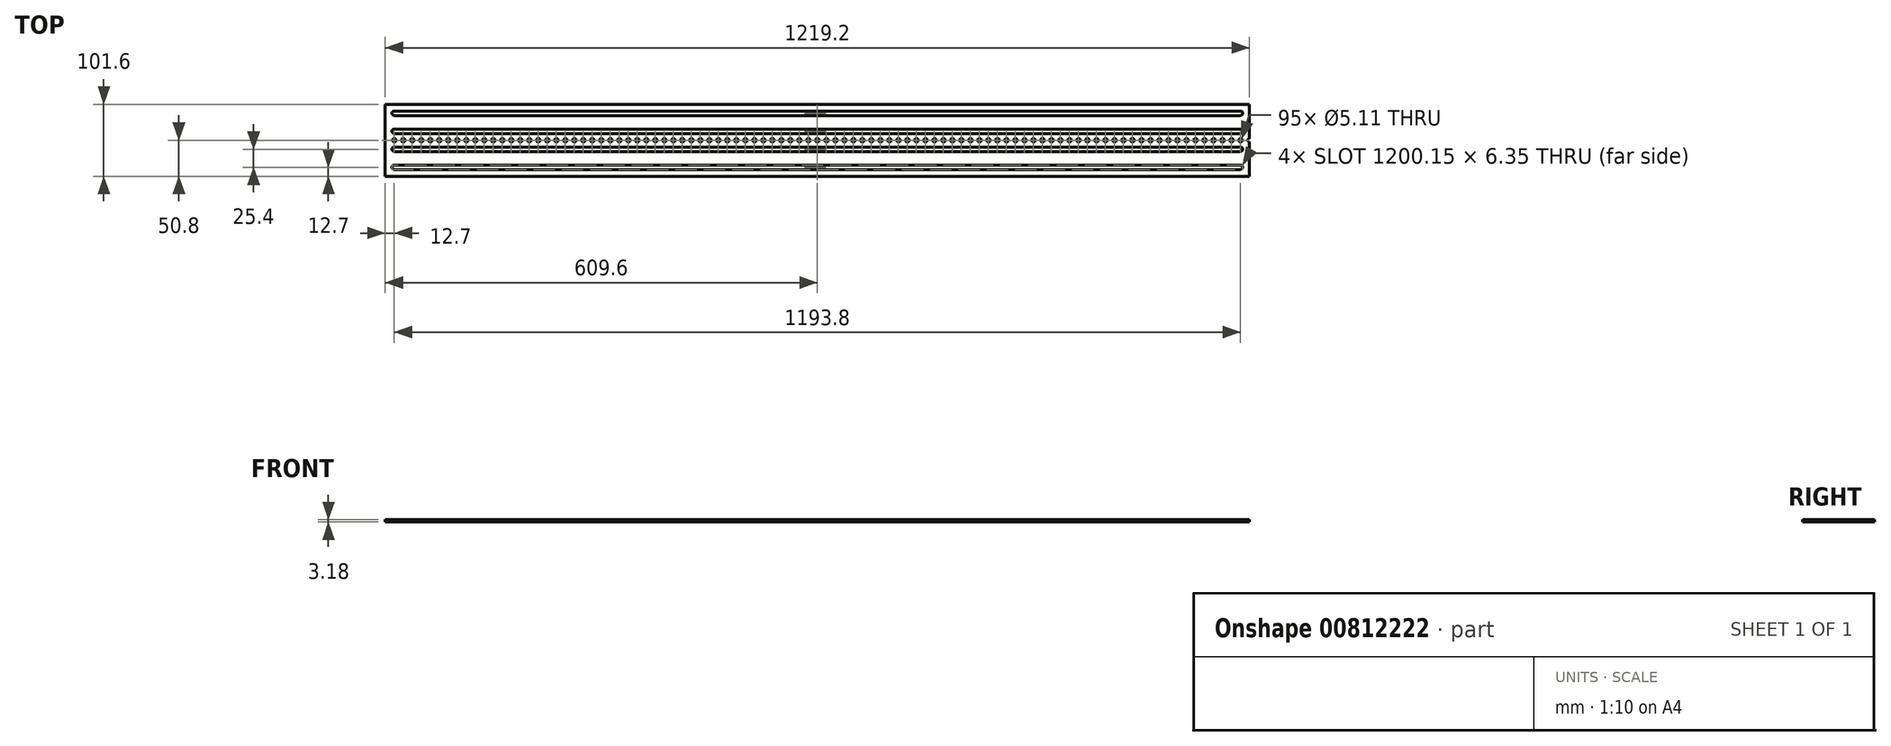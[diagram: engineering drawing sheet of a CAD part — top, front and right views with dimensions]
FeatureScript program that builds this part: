
annotation { "Feature Type Name" : "Feature", "Feature Type Description" : "" }
export const myFeature = defineFeature(function(context is Context, id is Id, definition is map)
    precondition{}
    {
        {
            var Q0;
            Q0=qCreatedBy(makeId("Top.planeOp"),FACE);
            var sketch = newSketch(context, id + "F0", { "sketchPlane" : qUnion([Q0])});
            skLineSegment(sketch, "E0.bottom", {"start": v(-609.6, -50.8) * mm, "end": v(609.6, -50.8) * mm});
            skLineSegment(sketch, "E0.top", {"start": v(-609.6, 50.8) * mm, "end": v(609.6, 50.8) * mm});
            skLineSegment(sketch, "E0.left", {"start": v(-609.6, -50.8) * mm, "end": v(-609.6, 50.8) * mm});
            skLineSegment(sketch, "E0.right", {"start": v(609.6, -50.8) * mm, "end": v(609.6, 50.8) * mm});
            skPoint(sketch, "E0.middle", {"position": v(0, 0) * mm});
            skLineSegment(sketch, "E1", {"start": v(-609.6, 25.4) * mm, "end": v(609.6, 25.4) * mm, "construction": true});
            skLineSegment(sketch, "E2", {"start": v(609.6, -25.4) * mm, "end": v(-609.6, -25.4) * mm, "construction": true});
            skLineSegment(sketch, "E3", {"start": v(0, -25.4) * mm, "end": v(0, 25.4) * mm, "construction": true});
            skLineSegment(sketch, "E4.bottom", {"start": v(-596.9, 12.7) * mm, "end": v(596.9, 12.7) * mm, "construction": true});
            skLineSegment(sketch, "E4.top", {"start": v(-596.9, -12.7) * mm, "end": v(596.9, -12.7) * mm, "construction": true});
            skLineSegment(sketch, "E4.left", {"start": v(-596.9, 12.7) * mm, "end": v(-596.9, -12.7) * mm, "construction": true});
            skLineSegment(sketch, "E4.right", {"start": v(596.9, 12.7) * mm, "end": v(596.9, -12.7) * mm, "construction": true});
            skArc(sketch, "E5", {"start": v(-596.9, 15.88) * mm, "mid": v(-600.08, 12.7) * mm, "end": v(-596.9, 9.53) * mm});
            skArc(sketch, "E6", {"start": v(-596.9, -9.53) * mm, "mid": v(-600.08, -12.7) * mm, "end": v(-596.9, -15.88) * mm});
            skArc(sketch, "E7", {"start": v(596.9, 9.53) * mm, "mid": v(600.08, 12.7) * mm, "end": v(596.9, 15.88) * mm});
            skArc(sketch, "E8", {"start": v(596.9, -15.88) * mm, "mid": v(600.08, -12.7) * mm, "end": v(596.9, -9.53) * mm});
            skLineSegment(sketch, "E9", {"start": v(596.9, 15.88) * mm, "end": v(-596.9, 15.87) * mm});
            skLineSegment(sketch, "E10", {"start": v(-596.9, 9.52) * mm, "end": v(596.9, 9.53) * mm});
            skLineSegment(sketch, "E11", {"start": v(-596.9, -9.53) * mm, "end": v(596.9, -9.53) * mm});
            skLineSegment(sketch, "E12", {"start": v(596.9, -15.88) * mm, "end": v(-596.9, -15.88) * mm});
            skCircle(sketch, "E13", {"center": v(-596.9, 0) * mm, "radius": 2.55 * mm});
            skCircle(sketch, "E14.1.0.0", {"center": v(-584.2, 0) * mm, "radius": 2.55 * mm});
            skCircle(sketch, "E14.2.0.0", {"center": v(-571.5, 0) * mm, "radius": 2.55 * mm});
            skCircle(sketch, "E14.3.0.0", {"center": v(-558.8, 0) * mm, "radius": 2.55 * mm});
            skCircle(sketch, "E14.4.0.0", {"center": v(-546.1, 0) * mm, "radius": 2.55 * mm});
            skCircle(sketch, "E14.5.0.0", {"center": v(-533.4, 0) * mm, "radius": 2.55 * mm});
            skCircle(sketch, "E14.6.0.0", {"center": v(-520.7, 0) * mm, "radius": 2.55 * mm});
            skCircle(sketch, "E14.7.0.0", {"center": v(-508, 0) * mm, "radius": 2.55 * mm});
            skCircle(sketch, "E14.8.0.0", {"center": v(-495.3, 0) * mm, "radius": 2.55 * mm});
            skCircle(sketch, "E14.9.0.0", {"center": v(-482.6, 0) * mm, "radius": 2.55 * mm});
            skCircle(sketch, "E14.10.0.0", {"center": v(-469.9, 0) * mm, "radius": 2.55 * mm});
            skCircle(sketch, "E14.11.0.0", {"center": v(-457.2, 0) * mm, "radius": 2.55 * mm});
            skCircle(sketch, "E14.12.0.0", {"center": v(-444.5, 0) * mm, "radius": 2.55 * mm});
            skCircle(sketch, "E14.13.0.0", {"center": v(-431.8, 0) * mm, "radius": 2.55 * mm});
            skCircle(sketch, "E14.14.0.0", {"center": v(-419.1, 0) * mm, "radius": 2.55 * mm});
            skCircle(sketch, "E14.15.0.0", {"center": v(-406.4, 0) * mm, "radius": 2.55 * mm});
            skCircle(sketch, "E14.16.0.0", {"center": v(-393.7, 0) * mm, "radius": 2.55 * mm});
            skCircle(sketch, "E14.17.0.0", {"center": v(-381, 0) * mm, "radius": 2.55 * mm});
            skCircle(sketch, "E14.18.0.0", {"center": v(-368.3, 0) * mm, "radius": 2.55 * mm});
            skCircle(sketch, "E14.19.0.0", {"center": v(-355.6, 0) * mm, "radius": 2.55 * mm});
            skCircle(sketch, "E14.20.0.0", {"center": v(-342.9, 0) * mm, "radius": 2.55 * mm});
            skCircle(sketch, "E14.21.0.0", {"center": v(-330.2, 0) * mm, "radius": 2.55 * mm});
            skCircle(sketch, "E14.22.0.0", {"center": v(-317.5, 0) * mm, "radius": 2.55 * mm});
            skCircle(sketch, "E14.23.0.0", {"center": v(-304.8, 0) * mm, "radius": 2.55 * mm});
            skCircle(sketch, "E14.24.0.0", {"center": v(-292.1, 0) * mm, "radius": 2.55 * mm});
            skCircle(sketch, "E14.25.0.0", {"center": v(-279.4, 0) * mm, "radius": 2.55 * mm});
            skCircle(sketch, "E14.26.0.0", {"center": v(-266.7, 0) * mm, "radius": 2.55 * mm});
            skCircle(sketch, "E14.27.0.0", {"center": v(-254, 0) * mm, "radius": 2.55 * mm});
            skCircle(sketch, "E14.28.0.0", {"center": v(-241.3, 0) * mm, "radius": 2.55 * mm});
            skCircle(sketch, "E14.29.0.0", {"center": v(-228.6, 0) * mm, "radius": 2.55 * mm});
            skCircle(sketch, "E14.30.0.0", {"center": v(-215.9, 0) * mm, "radius": 2.55 * mm});
            skCircle(sketch, "E14.31.0.0", {"center": v(-203.2, 0) * mm, "radius": 2.55 * mm});
            skCircle(sketch, "E14.32.0.0", {"center": v(-190.5, 0) * mm, "radius": 2.55 * mm});
            skCircle(sketch, "E14.33.0.0", {"center": v(-177.8, 0) * mm, "radius": 2.55 * mm});
            skCircle(sketch, "E14.34.0.0", {"center": v(-165.1, 0) * mm, "radius": 2.55 * mm});
            skCircle(sketch, "E14.35.0.0", {"center": v(-152.4, 0) * mm, "radius": 2.55 * mm});
            skCircle(sketch, "E14.36.0.0", {"center": v(-139.7, 0) * mm, "radius": 2.55 * mm});
            skCircle(sketch, "E14.37.0.0", {"center": v(-127, 0) * mm, "radius": 2.55 * mm});
            skCircle(sketch, "E14.38.0.0", {"center": v(-114.3, 0) * mm, "radius": 2.55 * mm});
            skCircle(sketch, "E14.39.0.0", {"center": v(-101.6, 0) * mm, "radius": 2.55 * mm});
            skCircle(sketch, "E14.40.0.0", {"center": v(-88.9, 0) * mm, "radius": 2.55 * mm});
            skCircle(sketch, "E14.41.0.0", {"center": v(-76.2, 0) * mm, "radius": 2.55 * mm});
            skCircle(sketch, "E14.42.0.0", {"center": v(-63.5, 0) * mm, "radius": 2.55 * mm});
            skCircle(sketch, "E14.43.0.0", {"center": v(-50.8, 0) * mm, "radius": 2.55 * mm});
            skCircle(sketch, "E14.44.0.0", {"center": v(-38.1, 0) * mm, "radius": 2.55 * mm});
            skCircle(sketch, "E14.45.0.0", {"center": v(-25.4, 0) * mm, "radius": 2.55 * mm});
            skCircle(sketch, "E14.46.0.0", {"center": v(-12.7, 0) * mm, "radius": 2.55 * mm});
            skCircle(sketch, "E14.47.0.0", {"center": v(0, 0) * mm, "radius": 2.55 * mm});
            skCircle(sketch, "E14.48.0.0", {"center": v(12.7, 0) * mm, "radius": 2.55 * mm});
            skCircle(sketch, "E14.49.0.0", {"center": v(25.4, 0) * mm, "radius": 2.55 * mm});
            skCircle(sketch, "E14.50.0.0", {"center": v(38.1, 0) * mm, "radius": 2.55 * mm});
            skCircle(sketch, "E14.51.0.0", {"center": v(50.8, 0) * mm, "radius": 2.55 * mm});
            skCircle(sketch, "E14.52.0.0", {"center": v(63.5, 0) * mm, "radius": 2.55 * mm});
            skCircle(sketch, "E14.53.0.0", {"center": v(76.2, 0) * mm, "radius": 2.55 * mm});
            skCircle(sketch, "E14.54.0.0", {"center": v(88.9, 0) * mm, "radius": 2.55 * mm});
            skCircle(sketch, "E14.55.0.0", {"center": v(101.6, 0) * mm, "radius": 2.55 * mm});
            skCircle(sketch, "E14.56.0.0", {"center": v(114.3, 0) * mm, "radius": 2.55 * mm});
            skCircle(sketch, "E14.57.0.0", {"center": v(127, 0) * mm, "radius": 2.55 * mm});
            skCircle(sketch, "E14.58.0.0", {"center": v(139.7, 0) * mm, "radius": 2.55 * mm});
            skCircle(sketch, "E14.59.0.0", {"center": v(152.4, 0) * mm, "radius": 2.55 * mm});
            skCircle(sketch, "E14.60.0.0", {"center": v(165.1, 0) * mm, "radius": 2.55 * mm});
            skCircle(sketch, "E14.61.0.0", {"center": v(177.8, 0) * mm, "radius": 2.55 * mm});
            skCircle(sketch, "E14.62.0.0", {"center": v(190.5, 0) * mm, "radius": 2.55 * mm});
            skCircle(sketch, "E14.63.0.0", {"center": v(203.2, 0) * mm, "radius": 2.55 * mm});
            skCircle(sketch, "E14.64.0.0", {"center": v(215.9, 0) * mm, "radius": 2.55 * mm});
            skCircle(sketch, "E14.65.0.0", {"center": v(228.6, 0) * mm, "radius": 2.55 * mm});
            skCircle(sketch, "E14.66.0.0", {"center": v(241.3, 0) * mm, "radius": 2.55 * mm});
            skCircle(sketch, "E14.67.0.0", {"center": v(254, 0) * mm, "radius": 2.55 * mm});
            skCircle(sketch, "E14.68.0.0", {"center": v(266.7, 0) * mm, "radius": 2.55 * mm});
            skCircle(sketch, "E14.69.0.0", {"center": v(279.4, 0) * mm, "radius": 2.55 * mm});
            skCircle(sketch, "E14.70.0.0", {"center": v(292.1, 0) * mm, "radius": 2.55 * mm});
            skCircle(sketch, "E14.71.0.0", {"center": v(304.8, 0) * mm, "radius": 2.55 * mm});
            skCircle(sketch, "E14.72.0.0", {"center": v(317.5, 0) * mm, "radius": 2.55 * mm});
            skCircle(sketch, "E14.73.0.0", {"center": v(330.2, 0) * mm, "radius": 2.55 * mm});
            skCircle(sketch, "E14.74.0.0", {"center": v(342.9, 0) * mm, "radius": 2.55 * mm});
            skCircle(sketch, "E14.75.0.0", {"center": v(355.6, 0) * mm, "radius": 2.55 * mm});
            skCircle(sketch, "E14.76.0.0", {"center": v(368.3, 0) * mm, "radius": 2.55 * mm});
            skCircle(sketch, "E14.77.0.0", {"center": v(381, 0) * mm, "radius": 2.55 * mm});
            skCircle(sketch, "E14.78.0.0", {"center": v(393.7, 0) * mm, "radius": 2.55 * mm});
            skCircle(sketch, "E14.79.0.0", {"center": v(406.4, 0) * mm, "radius": 2.55 * mm});
            skCircle(sketch, "E14.80.0.0", {"center": v(419.1, 0) * mm, "radius": 2.55 * mm});
            skCircle(sketch, "E14.81.0.0", {"center": v(431.8, 0) * mm, "radius": 2.55 * mm});
            skCircle(sketch, "E14.82.0.0", {"center": v(444.5, 0) * mm, "radius": 2.55 * mm});
            skCircle(sketch, "E14.83.0.0", {"center": v(457.2, 0) * mm, "radius": 2.55 * mm});
            skCircle(sketch, "E14.84.0.0", {"center": v(469.9, 0) * mm, "radius": 2.55 * mm});
            skCircle(sketch, "E14.85.0.0", {"center": v(482.6, 0) * mm, "radius": 2.55 * mm});
            skCircle(sketch, "E14.86.0.0", {"center": v(495.3, 0) * mm, "radius": 2.55 * mm});
            skCircle(sketch, "E14.87.0.0", {"center": v(508, 0) * mm, "radius": 2.55 * mm});
            skCircle(sketch, "E14.88.0.0", {"center": v(520.7, 0) * mm, "radius": 2.55 * mm});
            skCircle(sketch, "E14.89.0.0", {"center": v(533.4, 0) * mm, "radius": 2.55 * mm});
            skCircle(sketch, "E14.90.0.0", {"center": v(546.1, 0) * mm, "radius": 2.55 * mm});
            skCircle(sketch, "E14.91.0.0", {"center": v(558.8, 0) * mm, "radius": 2.55 * mm});
            skCircle(sketch, "E14.92.0.0", {"center": v(571.5, 0) * mm, "radius": 2.55 * mm});
            skCircle(sketch, "E14.93.0.0", {"center": v(584.2, 0) * mm, "radius": 2.55 * mm});
            skCircle(sketch, "E14.94.0.0", {"center": v(596.9, 0) * mm, "radius": 2.55 * mm});
            skCircle(sketch, "E14.95.0.0", {"center": v(609.6, 0) * mm, "radius": 2.55 * mm});
            skCircle(sketch, "E14.96.0.0", {"center": v(622.3, 0) * mm, "radius": 2.55 * mm});
            skCircle(sketch, "E14.97.0.0", {"center": v(635, 0) * mm, "radius": 2.55 * mm});
            skCircle(sketch, "E14.98.0.0", {"center": v(647.7, 0) * mm, "radius": 2.55 * mm});
            skCircle(sketch, "E14.99.0.0", {"center": v(660.4, 0) * mm, "radius": 2.55 * mm});
            skLineSegment(sketch, "E14.direction1", {"start": v(-596.9, 0) * mm, "end": v(-584.2, 0) * mm, "construction": true});
            skCircle(sketch, "E15.95.0.0", {"center": v(618.07, 0) * mm, "radius": 2.55 * mm});
            skCircle(sketch, "E15.98.0.0", {"center": v(639.23, 0) * mm, "radius": 2.55 * mm});
            skLineSegment(sketch, "E16", {"start": v(639.23, 0) * mm, "end": v(660.4, 0) * mm, "construction": true});
            skLineSegment(sketch, "E17", {"start": v(618.07, 0) * mm, "end": v(639.23, 0) * mm, "construction": true});
            skLineSegment(sketch, "E18", {"start": v(596.9, 0) * mm, "end": v(618.07, 0) * mm, "construction": true});
            skLineSegment(sketch, "E19", {"start": v(-596.9, 38.1) * mm, "end": v(596.9, 38.1) * mm, "construction": true});
            skArc(sketch, "E20", {"start": v(596.9, 34.93) * mm, "mid": v(600.07, 38.1) * mm, "end": v(596.9, 41.27) * mm});
            skLineSegment(sketch, "E21", {"start": v(596.9, 41.28) * mm, "end": v(-596.9, 41.27) * mm});
            skLineSegment(sketch, "E22", {"start": v(-596.9, 34.92) * mm, "end": v(596.9, 34.93) * mm});
            skLineSegment(sketch, "E23", {"start": v(0, 25.4) * mm, "end": v(0, 50.8) * mm, "construction": true});
            skPoint(sketch, "E24", {"position": v(0, 38.1) * mm});
            skLineSegment(sketch, "E25", {"start": v(-596.9, 0) * mm, "end": v(596.9, 0) * mm, "construction": true});
            skLineSegment(sketch, "E26.MirrorCS", {"start": v(-596.9, -34.93) * mm, "end": v(596.9, -34.92) * mm});
            skLineSegment(sketch, "E27.MirrorCS", {"start": v(-596.9, -38.1) * mm, "end": v(596.9, -38.1) * mm, "construction": true});
            skArc(sketch, "E28.MirrorCS", {"start": v(596.9, -34.93) * mm, "mid": v(600.07, -38.1) * mm, "end": v(596.9, -41.27) * mm});
            skLineSegment(sketch, "E29.MirrorCS", {"start": v(596.9, -41.27) * mm, "end": v(-596.9, -41.28) * mm});
            skArc(sketch, "E30", {"start": v(-596.9, 41.28) * mm, "mid": v(-600.08, 38.1) * mm, "end": v(-596.9, 34.93) * mm});
            skArc(sketch, "E31", {"start": v(-596.9, -34.93) * mm, "mid": v(-600.08, -38.1) * mm, "end": v(-596.9, -41.28) * mm});
            skSolve(sketch);
        }
        {
            var Q0;
            Q0=makeQuery(id+"F0.imprint","IMPRINT",FACE,{"disambiguationData":[TD([[makeQuery(id+"F0.imprint","IMPRINT",EDGE,{"derivedFrom":sQuery(id+"F0.wireOp",EDGE,"E0.bottom")}),1.0]])]});
            extrude(context, id + "F1", {"entities" : qUnion([Q0]), "depth" : 3.17 * mm, "offsetDistance" : 25.4 * mm});
        }
    });
